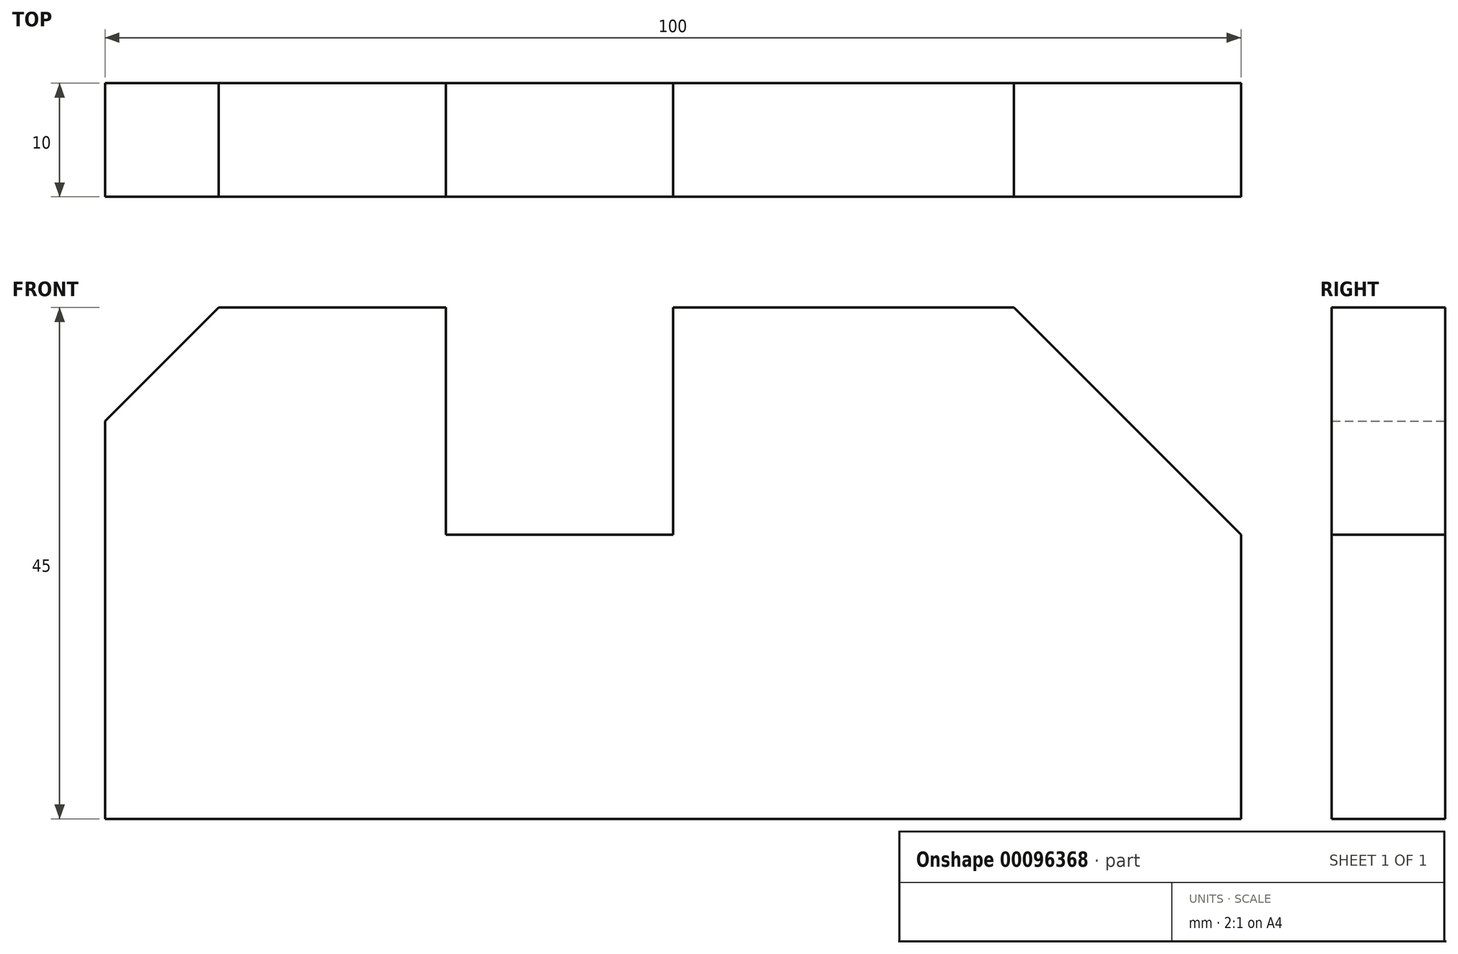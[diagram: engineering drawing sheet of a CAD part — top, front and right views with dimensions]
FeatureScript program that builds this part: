
annotation { "Feature Type Name" : "Feature", "Feature Type Description" : "" }
export const myFeature = defineFeature(function(context is Context, id is Id, definition is map)
    precondition{}
    {
        {
            var Q0;
            Q0=qCreatedBy(makeId("Front.planeOp"),FACE);
            var sketch = newSketch(context, id + "F0", { "sketchPlane" : qUnion([Q0])});
            skLineSegment(sketch, "E0", {"start": v(0, 0) * mm, "end": v(100, 0) * mm});
            skLineSegment(sketch, "E1", {"start": v(100, 0) * mm, "end": v(100, 25) * mm});
            skLineSegment(sketch, "E2", {"start": v(100, 25) * mm, "end": v(80, 45) * mm});
            skLineSegment(sketch, "E3", {"start": v(80, 45) * mm, "end": v(50, 45) * mm});
            skLineSegment(sketch, "E4", {"start": v(50, 45) * mm, "end": v(50, 25) * mm});
            skLineSegment(sketch, "E5", {"start": v(50, 25) * mm, "end": v(30, 25) * mm});
            skLineSegment(sketch, "E6", {"start": v(30, 25) * mm, "end": v(30, 45) * mm});
            skLineSegment(sketch, "E7", {"start": v(30, 45) * mm, "end": v(10, 45) * mm});
            skLineSegment(sketch, "E8", {"start": v(10, 45) * mm, "end": v(0, 35) * mm});
            skLineSegment(sketch, "E9", {"start": v(0, 35) * mm, "end": v(0, 0) * mm});
            skSolve(sketch);
        }
        {
            var Q0;
            Q0=makeQuery(id+"F0.imprint","IMPRINT",FACE,{"disambiguationData":[TD([[makeQuery(id+"F0.imprint","IMPRINT",EDGE,{"derivedFrom":sQuery(id+"F0.wireOp",EDGE,"E0")}),1.0]])]});
            extrude(context, id + "F1", {"entities" : qUnion([Q0]), "depth" : 10 * mm});
        }
    });
